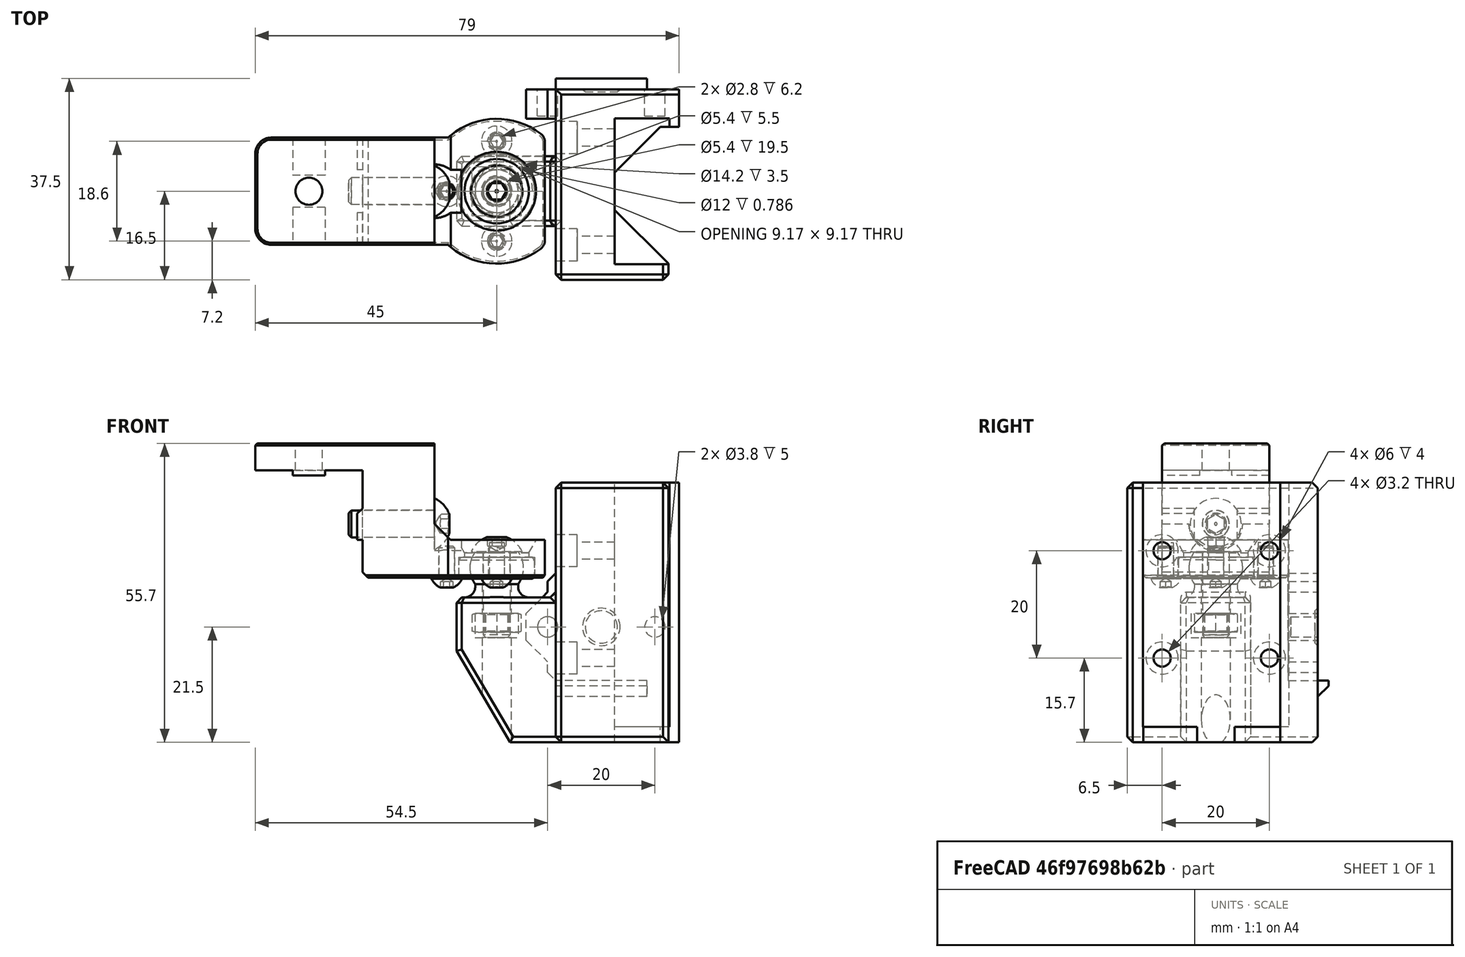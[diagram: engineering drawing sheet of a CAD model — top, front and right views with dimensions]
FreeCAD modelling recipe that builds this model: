
FCSTD DOCUMENT  (FreeCAD 0.19R24291 (Git))
Label: Trident_to_chip
License: All rights reserved
LicenseURL: http://en.wikipedia.org/wiki/All_rights_reserved
objects: Part::FeaturePython×9, App::FeaturePython×8
note: 9 computed .brp shape members not serialized (recipe doc carries the construction recipe); baked Part::Feature solids carry a one-line shape summary decoded from their .brp

FEATURE [Part::FeaturePython] b_chip_trident_001_  label="chip_trident_001"  # a2plus imported part (geometry in sourceFile) (typed FeaturePython)
  Placement = pos=(0,0,0) rot=(0,0,1;3.14159rad)
  a2p_Version = V0.1
  fixedPosition = true
  objectType = a2pPart
  sourceFile = .\..\Downloads\Trident_Assembly.step\chip_trident.FCStd
  subassemblyImport = false
  timeLastImport = 1.63232e+09
  updateColors = true
FEATURE [Part::FeaturePython] b_chip_trident2_001_  label="chip_trident2_001"  # a2plus imported part (geometry in sourceFile) (typed FeaturePython)
  Placement = pos=(2.98e-13,1.02e-13,7.30001) rot=(0,0,1;0rad)
  a2p_Version = V0.1
  fixedPosition = false
  objectType = a2pPart
  sourceFile = .\..\Downloads\Trident_Assembly.step\chip_trident2.FCStd
  subassemblyImport = false
  timeLastImport = 1.63239e+09
  updateColors = true
FEATURE [Part::FeaturePython] b_EGLM_05_11_001_  label="EGLM_05_11_001"  # a2plus imported part (geometry in sourceFile) (typed FeaturePython)
  Placement = pos=(-22,5.14284e-08,36.8) rot=(1,0,0;1.5708rad)
  a2p_Version = V0.1
  fixedPosition = false
  objectType = a2pPart
  sourceFile = .\..\Downloads\igus_20210923_102344\EGLM_05_1.stp
  subassemblyImport = false
  timeLastImport = 1.63239e+09
  updateColors = true
FEATURE [App::FeaturePython] axisCoincident_001  label="axisCoincident_001__chip_trident_001"  # a2plus constraint (typed FeaturePython)
  Object1 = b_EGLM_05_11_001_
  Object2 = b_chip_trident_001_
  ParentTreeObject = -> b_EGLM_05_11_001_
  SubElement1 = Edge10
  SubElement2 = Edge216
  Suppressed = false
  Type = axial
  directionConstraint = 0
  lockRotation = false
FEATURE [App::FeaturePython] axisCoincident_001_mirror  label="axisCoincident_001__EGLM_05_11_001"  # a2plus constraint (typed FeaturePython)
  Object1 = b_EGLM_05_11_001_
  Object2 = b_chip_trident_001_
  ParentTreeObject = -> b_chip_trident_001_
  SubElement1 = Edge10
  SubElement2 = Edge216
  Suppressed = false
  Type = axial
  directionConstraint = 0
  lockRotation = false
FEATURE [App::FeaturePython] planeCoincident_001  label="planeCoincident_001__chip_trident_001"  # a2plus constraint (typed FeaturePython)
  Object1 = b_EGLM_05_11_001_
  Object2 = b_chip_trident_001_
  ParentTreeObject = -> b_EGLM_05_11_001_
  SubElement1 = Face13
  SubElement2 = Face70
  Suppressed = false
  Type = plane
  directionConstraint = 1
  offset = 0
FEATURE [App::FeaturePython] planeCoincident_001_mirror  label="planeCoincident_001__EGLM_05_11_001"  # a2plus constraint (typed FeaturePython)
  Object1 = b_EGLM_05_11_001_
  Object2 = b_chip_trident_001_
  ParentTreeObject = -> b_chip_trident_001_
  SubElement1 = Face13
  SubElement2 = Face70
  Suppressed = false
  Type = plane
  directionConstraint = 1
  offset = 0
FEATURE [App::FeaturePython] axisCoincident_002  label="axisCoincident_002__EGLM_05_11_001"  # a2plus constraint (typed FeaturePython)
  Object1 = b_chip_trident2_001_
  Object2 = b_EGLM_05_11_001_
  ParentTreeObject = -> b_chip_trident2_001_
  SubElement1 = Edge66
  SubElement2 = Edge16
  Suppressed = false
  Type = axial
  directionConstraint = 0
  lockRotation = false
FEATURE [App::FeaturePython] axisCoincident_002_mirror  label="axisCoincident_002__chip_trident2_001"  # a2plus constraint (typed FeaturePython)
  Object1 = b_chip_trident2_001_
  Object2 = b_EGLM_05_11_001_
  ParentTreeObject = -> b_EGLM_05_11_001_
  SubElement1 = Edge66
  SubElement2 = Edge16
  Suppressed = false
  Type = axial
  directionConstraint = 0
  lockRotation = false
FEATURE [App::FeaturePython] planeCoincident_002  label="planeCoincident_002__EGLM_05_11_001"  # a2plus constraint (typed FeaturePython)
  Object1 = b_chip_trident2_001_
  Object2 = b_EGLM_05_11_001_
  ParentTreeObject = -> b_chip_trident2_001_
  SubElement1 = Face20
  SubElement2 = Face2
  Suppressed = false
  Type = plane
  directionConstraint = 1
  offset = 0
FEATURE [App::FeaturePython] planeCoincident_002_mirror  label="planeCoincident_002__chip_trident2_001"  # a2plus constraint (typed FeaturePython)
  Object1 = b_chip_trident2_001_
  Object2 = b_EGLM_05_11_001_
  ParentTreeObject = -> b_EGLM_05_11_001_
  SubElement1 = Face20
  SubElement2 = Face2
  Suppressed = false
  Type = plane
  directionConstraint = 1
  offset = 0
FEATURE [Part::FeaturePython] Screw  label="M5x16-Screw"  # Fasteners workbench fastener (typed FeaturePython)
  Placement = pos=(-33.5769,4e-15,45) rot=(0,1,0;1.5708rad)
  baseObject = -> b_chip_trident_001_ [Edge178]
  diameter = 3
  invert = true
  length = 12
  lengthCustom = 16
  matchOuter = false
  offset = 0
  thread = false
  type = 39
FEATURE [Part::FeaturePython] Screw001  label="M3x6-Screw"  # Fasteners workbench fastener (typed FeaturePython)
  Placement = pos=(-31.3,0,34.8) rot=(-1,0,0;3.14159rad)
  baseObject = -> b_chip_trident_001_ [Edge18]
  diameter = 1
  invert = false
  length = 0
  lengthCustom = 6
  matchOuter = true
  offset = 0.2
  thread = false
  type = 39
FEATURE [Part::FeaturePython] Screw002  label="M3x6-Screw003"  # Fasteners workbench fastener (typed FeaturePython)
  Placement = pos=(-22,9.3,34.8) rot=(-1,0,0;3.14159rad)
  baseObject = -> b_chip_trident_001_ [Edge143]
  diameter = 1
  invert = false
  length = 0
  lengthCustom = 6
  matchOuter = true
  offset = 6.7
  thread = false
  type = 39
FEATURE [Part::FeaturePython] Screw003  label="M3x6-Screw002"  # Fasteners workbench fastener (typed FeaturePython)
  Placement = pos=(-22,-9.3,34.8) rot=(-1,0,0;3.14159rad)
  baseObject = -> b_chip_trident_001_ [Edge151]
  diameter = 1
  invert = false
  length = 0
  lengthCustom = 6
  matchOuter = true
  offset = 6.7
  thread = false
  type = 39
FEATURE [Part::FeaturePython] Screw004  label="M5x16-Screw001"  # Fasteners workbench fastener (typed FeaturePython)
  Placement = pos=(-22,1.02857e-07,39.8) rot=(0,0,1;0rad)
  baseObject = -> b_EGLM_05_11_001_ [Edge16]
  diameter = 3
  invert = false
  length = 4
  lengthCustom = 16
  matchOuter = true
  offset = 0
  thread = false
  type = 39
FEATURE [Part::FeaturePython] Nut  label="M5-Nut"  # Fasteners workbench fastener (typed FeaturePython)
  Placement = pos=(-22,1.02e-13,28.3) rot=(-1,0,0;3.14159rad)
  baseObject = -> b_chip_trident2_001_ [Edge132]
  diameter = 7
  invert = false
  matchOuter = true
  offset = 0
  thread = false
  type = 7
